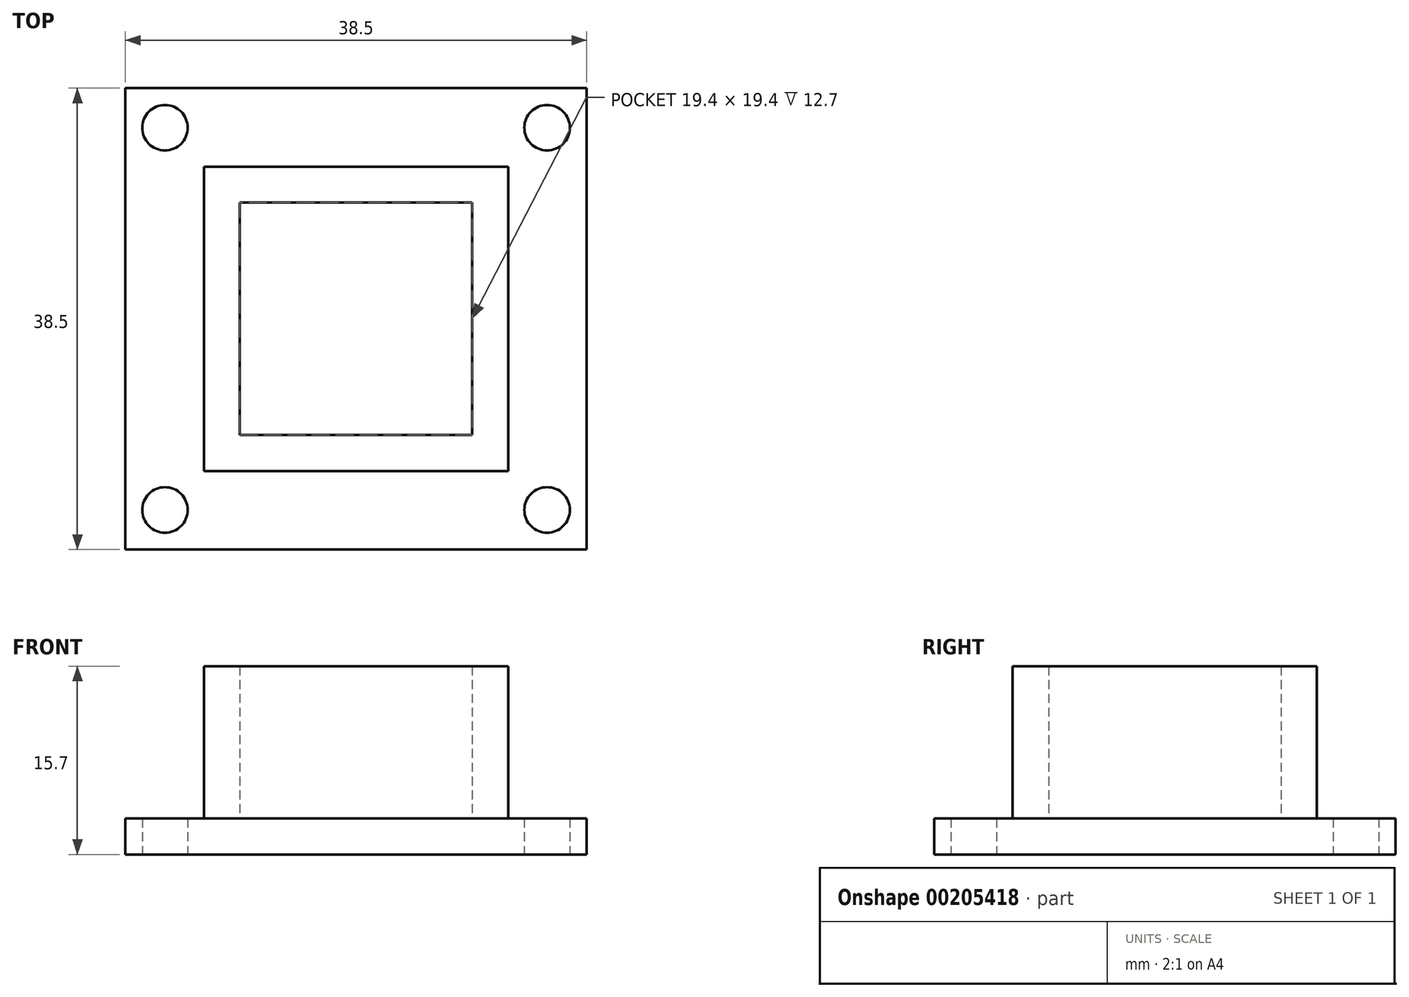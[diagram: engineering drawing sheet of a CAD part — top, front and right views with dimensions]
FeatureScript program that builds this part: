
annotation { "Feature Type Name" : "Feature", "Feature Type Description" : "" }
export const myFeature = defineFeature(function(context is Context, id is Id, definition is map)
    precondition{}
    {
        {
            var Q0;
            Q0=qCreatedBy(makeId("Top.planeOp"),FACE);
            var sketch = newSketch(context, id + "F0", { "sketchPlane" : qUnion([Q0])});
            skLineSegment(sketch, "E0", {"start": v(-19.25, 0) * mm, "end": v(-19.25, 19.25) * mm});
            skLineSegment(sketch, "E1", {"start": v(-19.25, 19.25) * mm, "end": v(19.25, 19.25) * mm});
            skLineSegment(sketch, "E2", {"start": v(19.25, 19.25) * mm, "end": v(19.25, -19.25) * mm});
            skLineSegment(sketch, "E3", {"start": v(19.25, -19.25) * mm, "end": v(-19.25, -19.25) * mm});
            skLineSegment(sketch, "E4", {"start": v(-19.25, -19.25) * mm, "end": v(-19.25, 19.25) * mm});
            skCircle(sketch, "E5", {"center": v(-15.95, 15.95) * mm, "radius": 1.9 * mm});
            skCircle(sketch, "E6", {"center": v(15.95, 15.95) * mm, "radius": 1.9 * mm});
            skCircle(sketch, "E7", {"center": v(15.95, -15.95) * mm, "radius": 1.9 * mm});
            skCircle(sketch, "E8", {"center": v(-15.95, -15.95) * mm, "radius": 1.9 * mm});
            skSolve(sketch);
        }
        {
            var Q0;
            {var subQ1=sQuery(id+"F0.wireOp",EDGE,"E1");Q0=makeQuery(id+"F0.imprint","IMPRINT",FACE,{"disambiguationData":[TD([[makeQuery(id+"F0.imprint","IMPRINT",EDGE,{"derivedFrom":subQ1}),-1.0]])]});}
            extrude(context, id + "F1", {"entities" : qUnion([Q0]), "depth" : 3 * mm});
        }
        {
            var Q0;
            Q0=makeQuery(id+"F1.opExtrude","CAP_FACE",FACE,{"disambiguationData":[OSD([sQuery(id+"F0.wireOp",EDGE,"E1"),sQuery(id+"F0.wireOp",EDGE,"E2"),sQuery(id+"F0.wireOp",EDGE,"E3"),sQuery(id+"F0.wireOp",EDGE,"E4"),sQuery(id+"F0.wireOp",EDGE,"E5"),sQuery(id+"F0.wireOp",EDGE,"E6"),sQuery(id+"F0.wireOp",EDGE,"E7"),sQuery(id+"F0.wireOp",EDGE,"E8")])],"isStart":false});
            var sketch = newSketch(context, id + "F2", { "sketchPlane" : qUnion([Q0])});
            skLineSegment(sketch, "E9", {"start": v(-12.7, 12.7) * mm, "end": v(12.7, 12.7) * mm});
            skLineSegment(sketch, "E10", {"start": v(12.7, 12.7) * mm, "end": v(12.7, -12.7) * mm});
            skLineSegment(sketch, "E11", {"start": v(12.7, -12.7) * mm, "end": v(-12.7, -12.7) * mm});
            skLineSegment(sketch, "E12", {"start": v(-12.7, -12.7) * mm, "end": v(-12.7, 12.7) * mm});
            skLineSegment(sketch, "E13.0", {"start": v(-9.7, 9.7) * mm, "end": v(9.7, 9.7) * mm});
            skLineSegment(sketch, "E13.1", {"start": v(-9.7, -9.7) * mm, "end": v(-9.7, 9.7) * mm});
            skLineSegment(sketch, "E13.2", {"start": v(9.7, -9.7) * mm, "end": v(-9.7, -9.7) * mm});
            skLineSegment(sketch, "E13.3", {"start": v(9.7, 9.7) * mm, "end": v(9.7, -9.7) * mm});
            skSolve(sketch);
        }
        {
            var Q0;
            Q0=makeQuery(id+"F2.imprint","IMPRINT",FACE,{"disambiguationData":[TD([[makeQuery(id+"F2.imprint","IMPRINT",EDGE,{"derivedFrom":sQuery(id+"F2.wireOp",EDGE,"E9")}),-1.0]])]});
            extrude(context, id + "F3", {"entities" : qUnion([Q0]), "operationType" : NewBodyOperationType.ADD, "depth" : 12.7 * mm});
        }
    });
